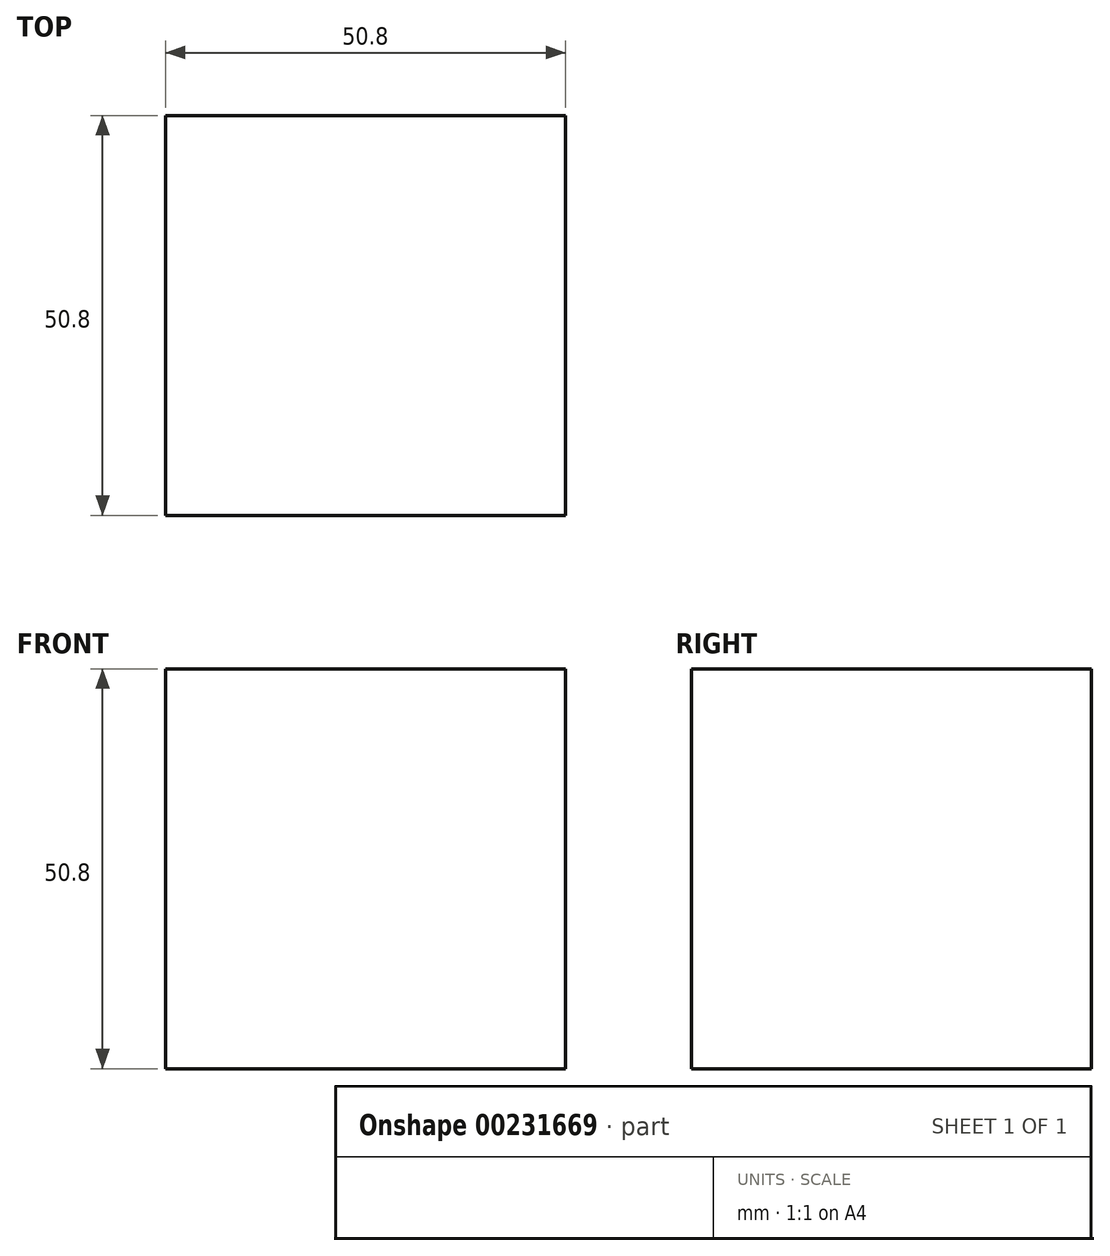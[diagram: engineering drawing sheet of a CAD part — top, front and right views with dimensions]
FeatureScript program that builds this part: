
annotation { "Feature Type Name" : "Feature", "Feature Type Description" : "" }
export const myFeature = defineFeature(function(context is Context, id is Id, definition is map)
    precondition{}
    {
        {
            var Q0;
            Q0=qCreatedBy(makeId("Front.planeOp"),FACE);
            var sketch = newSketch(context, id + "F0", { "sketchPlane" : qUnion([Q0])});
            skLineSegment(sketch, "E0.bottom", {"start": v(-25.4, -25.4) * mm, "end": v(25.4, -25.4) * mm});
            skLineSegment(sketch, "E0.top", {"start": v(-25.4, 25.4) * mm, "end": v(25.4, 25.4) * mm});
            skLineSegment(sketch, "E0.left", {"start": v(-25.4, -25.4) * mm, "end": v(-25.4, 25.4) * mm});
            skLineSegment(sketch, "E0.right", {"start": v(25.4, -25.4) * mm, "end": v(25.4, 25.4) * mm});
            skPoint(sketch, "E0.middle", {"position": v(0, 0) * mm});
            skSolve(sketch);
        }
        {
            var Q0;
            Q0 = qSketchRegion(id + "F0", true);
            extrude(context, id + "F1", {"entities" : qUnion([Q0]), "depth" : 50.8 * mm});
        }
    });
